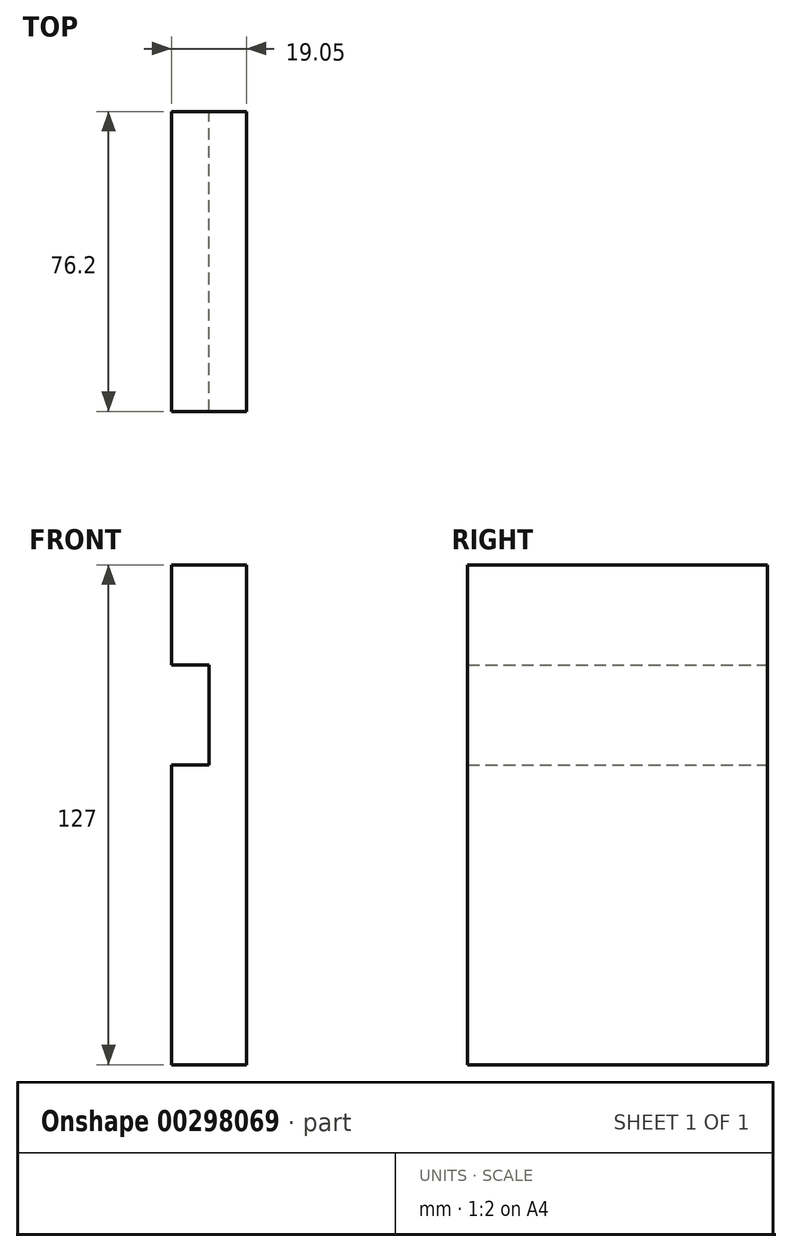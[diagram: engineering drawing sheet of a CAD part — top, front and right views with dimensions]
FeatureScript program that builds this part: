
annotation { "Feature Type Name" : "Feature", "Feature Type Description" : "" }
export const myFeature = defineFeature(function(context is Context, id is Id, definition is map)
    precondition{}
    {
        {
            var Q0;
            Q0=qCreatedBy(makeId("Front.planeOp"),FACE);
            var sketch = newSketch(context, id + "F0", { "sketchPlane" : qUnion([Q0])});
            skLineSegment(sketch, "E0", {"start": v(0, 0) * mm, "end": v(0, 127) * mm});
            skLineSegment(sketch, "E1", {"start": v(0, 127) * mm, "end": v(-19.05, 127) * mm});
            skLineSegment(sketch, "E2", {"start": v(-19.05, 127) * mm, "end": v(-19.05, 101.6) * mm});
            skLineSegment(sketch, "E3", {"start": v(-19.05, 101.6) * mm, "end": v(-9.52, 101.6) * mm});
            skLineSegment(sketch, "E4", {"start": v(-9.52, 101.6) * mm, "end": v(-9.52, 76.2) * mm});
            skLineSegment(sketch, "E5", {"start": v(-9.52, 76.2) * mm, "end": v(-19.05, 76.2) * mm});
            skLineSegment(sketch, "E6", {"start": v(-19.05, 76.2) * mm, "end": v(-19.05, 0) * mm});
            skLineSegment(sketch, "E7", {"start": v(-19.05, 0) * mm, "end": v(0, 0) * mm});
            skSolve(sketch);
        }
        {
            var Q0;
            Q0 = qSketchRegion(id + "F0", true);
            extrude(context, id + "F1", {"entities" : qUnion([Q0]), "depth" : 76.2 * mm});
        }
    });
